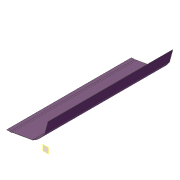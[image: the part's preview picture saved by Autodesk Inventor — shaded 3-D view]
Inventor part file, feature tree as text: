
AUTODESK INVENTOR PART (.ipt)
format: ipt  version: 2012 (Build 160160000, 160)  size: 90,624 bytes
history: native  units: in
note: dims shown in document units (in); Inventor stores cm internally (conversion verified against a paired STEP export)
features: plane x1, extrude x1, sketch x1
ambient origin geometry x8: Origin, YZ Plane, XZ Plane, XY Plane, X Axis, Y Axis, Z Axis, Center Point
bodies: Solid1 (feature_tree)
feature tree (3):
  plane  "Work Plane1"
  extrude  "Extrusion1"  Depth=0.0312in
  sketch  "Sketch1"  dims[d0=0.0312in d1=0.0312in d4=3.0in d8=0.0625in d9=0.0in d11=7.0in d12=1.0in d13=1.75in d14=15.0deg d15=0.0312in d16=1.0in d17=24.0in d18=0.0in]
